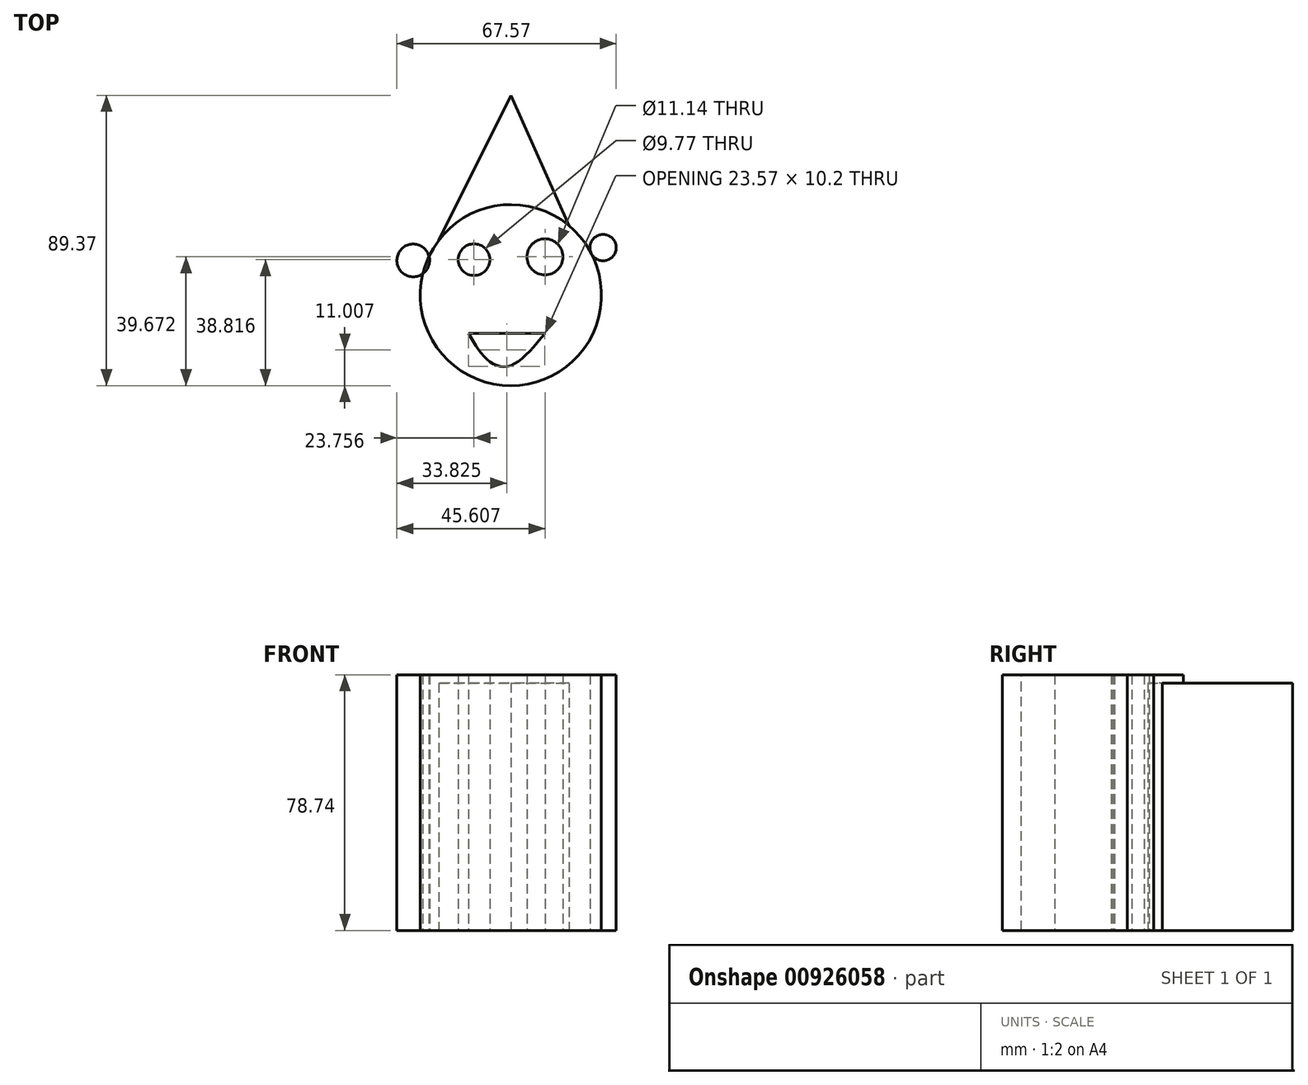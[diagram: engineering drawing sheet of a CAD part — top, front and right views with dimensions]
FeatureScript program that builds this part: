
annotation { "Feature Type Name" : "Feature", "Feature Type Description" : "" }
export const myFeature = defineFeature(function(context is Context, id is Id, definition is map)
    precondition{}
    {
        {
            var Q0;
            Q0=qCreatedBy(makeId("Top.planeOp"),FACE);
            var sketch = newSketch(context, id + "F0", { "sketchPlane" : qUnion([Q0])});
            skCircle(sketch, "E0", {"center": v(0, 0) * mm, "radius": 27.9 * mm});
            skLineSegment(sketch, "E1", {"start": v(-22.18, 16.91) * mm, "end": v(0, 61.48) * mm});
            skLineSegment(sketch, "E2", {"start": v(0, 61.48) * mm, "end": v(17.97, 21.33) * mm});
            skCircle(sketch, "E3", {"center": v(-11.35, 10.93) * mm, "radius": 4.89 * mm});
            skCircle(sketch, "E4", {"center": v(10.5, 11.78) * mm, "radius": 5.57 * mm});
            skLineSegment(sketch, "E5", {"start": v(-13.07, -11.78) * mm, "end": v(10.5, -11.78) * mm});
            skFitSpline(sketch, "E6", {"points": [v(-13.07, -11.78) * mm, v(-6.64, -20.35) * mm, v(0, -21.64) * mm, v(10.5, -11.78) * mm], "startDerivative": vector(17.44, -29.53) * mm, "endDerivative": vector(27, 32.98) * mm});
            skCircle(sketch, "E7", {"center": v(-30.07, 10.7) * mm, "radius": 5.04 * mm});
            skCircle(sketch, "E8", {"center": v(28.4, 14.63) * mm, "radius": 4.06 * mm});
            skSolve(sketch);
        }
        {
            var Q0;
            Q0=makeQuery(id+"F0.imprint","IMPRINT",FACE,{"disambiguationData":[TD([[makeQuery(id+"F0.imprint","IMPRINT",EDGE,{"derivedFrom":sQuery(id+"F0.wireOp",EDGE,"E3")}),-1.0]])]});
            var Q1;
            Q1=makeQuery(id+"F0.imprint","IMPRINT",FACE,{"disambiguationData":[TD([[makeQuery(id+"F0.imprint","IMPRINT",EDGE,{"derivedFrom":sQuery(id+"F0.wireOp",EDGE,"E8")}),1.0]])]});
            var Q2;
            {var subQ0=sQuery(id+"F0.wireOp",EDGE,"E7");var subQ1=sQuery(id+"F0.wireOp",EDGE,"E0");var subQ2=makeQuery(id+"F0.imprint","INTERSECT",VERTEX,{"disambiguationData":[OD(0.0)],"derivedFrom":[subQ1,subQ0]});Q2=makeQuery(id+"F0.imprint","IMPRINT",FACE,{"disambiguationData":[TD([[makeQuery(id+"F0.imprint","IMPRINT",EDGE,{"disambiguationData":[TD([[subQ2,-1.0]])],"derivedFrom":subQ1}),-1.0]])]});}
            extrude(context, id + "F1", {"entities" : qUnion([Q0, Q1, Q2]), "depth" : 2.54 * mm, "offsetDistance" : 25.4 * mm});
        }
        {
            var Q0;
            Q0=makeQuery(id+"F1.opExtrude","CAP_FACE",FACE,{"disambiguationData":[OSD([sQuery(id+"F0.wireOp",EDGE,"E0"),sQuery(id+"F0.wireOp",EDGE,"E7")])],"isStart":false});
            var Q1;
            Q1=makeQuery(id+"F1.opExtrude","CAP_FACE",FACE,{"disambiguationData":[OSD([sQuery(id+"F0.wireOp",EDGE,"E0"),sQuery(id+"F0.wireOp",EDGE,"E3"),sQuery(id+"F0.wireOp",EDGE,"E4"),sQuery(id+"F0.wireOp",EDGE,"E5"),sQuery(id+"F0.wireOp",EDGE,"E6"),sQuery(id+"F0.wireOp",EDGE,"E7")])],"isStart":false});
            var Q2;
            {var subQ0=sQuery(id+"F0.wireOp",EDGE,"E1");Q2=makeQuery(id+"F0.imprint","IMPRINT",FACE,{"disambiguationData":[TD([[makeQuery(id+"F0.imprint","IMPRINT",EDGE,{"derivedFrom":subQ0}),-1.0]])]});}
            var Q3;
            Q3=makeQuery(id+"F1.opExtrude","CAP_FACE",FACE,{"disambiguationData":[OSD([sQuery(id+"F0.wireOp",EDGE,"E8")])],"isStart":false});
            extrude(context, id + "F2", {"entities" : qUnion([Q0, Q1, Q2, Q3]), "operationType" : NewBodyOperationType.ADD, "depth" : 76.2 * mm, "offsetDistance" : 25.4 * mm});
        }
    });
